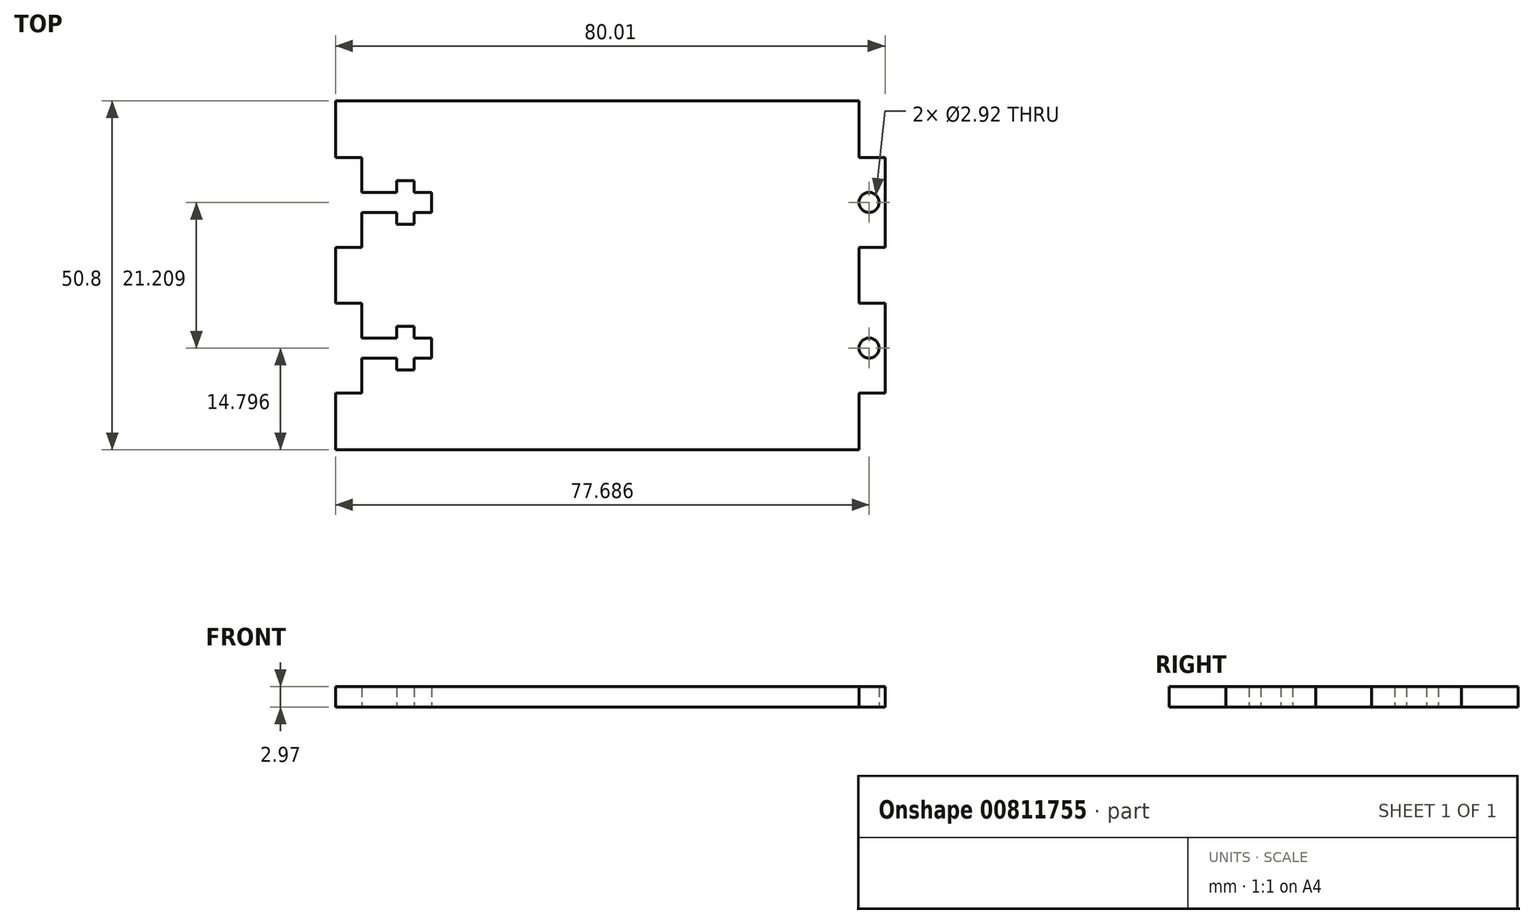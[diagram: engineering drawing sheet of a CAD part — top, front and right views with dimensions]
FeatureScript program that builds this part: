
annotation { "Feature Type Name" : "Feature", "Feature Type Description" : "" }
export const myFeature = defineFeature(function(context is Context, id is Id, definition is map)
    precondition{}
    {
        {
            var Q0;
            Q0=qCreatedBy(makeId("Top.planeOp"),FACE);
            var sketch = newSketch(context, id + "F0", { "sketchPlane" : qUnion([Q0])});
            skLineSegment(sketch, "E0.bottom", {"start": v(0, 0) * mm, "end": v(76.2, 0) * mm});
            skLineSegment(sketch, "E0.top", {"start": v(0, 50.8) * mm, "end": v(76.2, 50.8) * mm});
            skLineSegment(sketch, "E1", {"start": v(0, 8.26) * mm, "end": v(3.81, 8.26) * mm});
            skLineSegment(sketch, "E2", {"start": v(3.81, 8.26) * mm, "end": v(3.81, 13.34) * mm});
            skLineSegment(sketch, "E3", {"start": v(3.81, 13.34) * mm, "end": v(8.9, 13.34) * mm});
            skLineSegment(sketch, "E4", {"start": v(8.9, 13.34) * mm, "end": v(8.9, 11.6) * mm});
            skLineSegment(sketch, "E5", {"start": v(8.9, 11.6) * mm, "end": v(11.43, 11.6) * mm});
            skLineSegment(sketch, "E6", {"start": v(11.43, 11.6) * mm, "end": v(11.43, 13.34) * mm});
            skLineSegment(sketch, "E7", {"start": v(11.43, 13.34) * mm, "end": v(13.97, 13.34) * mm});
            skLineSegment(sketch, "E8", {"start": v(13.97, 13.34) * mm, "end": v(13.97, 16.26) * mm});
            skLineSegment(sketch, "E9", {"start": v(13.97, 16.26) * mm, "end": v(11.43, 16.26) * mm});
            skLineSegment(sketch, "E10", {"start": v(11.43, 16.26) * mm, "end": v(11.43, 17.98) * mm});
            skLineSegment(sketch, "E11", {"start": v(11.43, 17.98) * mm, "end": v(8.9, 17.98) * mm});
            skLineSegment(sketch, "E12", {"start": v(8.9, 17.98) * mm, "end": v(8.9, 16.26) * mm});
            skLineSegment(sketch, "E13", {"start": v(8.9, 16.26) * mm, "end": v(3.81, 16.26) * mm});
            skLineSegment(sketch, "E14", {"start": v(3.81, 16.26) * mm, "end": v(3.81, 21.34) * mm});
            skLineSegment(sketch, "E15", {"start": v(3.81, 21.34) * mm, "end": v(0, 21.34) * mm});
            skLineSegment(sketch, "E16", {"start": v(0, 0) * mm, "end": v(0, 8.26) * mm});
            skLineSegment(sketch, "E17", {"start": v(0, 50.8) * mm, "end": v(0, 42.55) * mm});
            skLineSegment(sketch, "E18", {"start": v(0, 42.55) * mm, "end": v(3.81, 42.55) * mm});
            skLineSegment(sketch, "E19", {"start": v(3.81, 42.54) * mm, "end": v(3.81, 37.46) * mm});
            skLineSegment(sketch, "E20", {"start": v(3.81, 37.46) * mm, "end": v(8.89, 37.46) * mm});
            skLineSegment(sketch, "E21", {"start": v(8.89, 37.46) * mm, "end": v(8.89, 39.2) * mm});
            skLineSegment(sketch, "E22", {"start": v(8.89, 39.2) * mm, "end": v(11.43, 39.2) * mm});
            skLineSegment(sketch, "E23", {"start": v(11.43, 39.2) * mm, "end": v(11.43, 37.46) * mm});
            skLineSegment(sketch, "E24", {"start": v(11.43, 37.46) * mm, "end": v(13.97, 37.46) * mm});
            skLineSegment(sketch, "E25", {"start": v(13.97, 37.46) * mm, "end": v(13.97, 34.54) * mm});
            skLineSegment(sketch, "E26", {"start": v(13.97, 34.54) * mm, "end": v(11.43, 34.54) * mm});
            skLineSegment(sketch, "E27", {"start": v(11.43, 34.54) * mm, "end": v(11.43, 32.82) * mm});
            skLineSegment(sketch, "E28", {"start": v(11.43, 32.82) * mm, "end": v(8.89, 32.82) * mm});
            skLineSegment(sketch, "E29", {"start": v(8.89, 32.82) * mm, "end": v(8.89, 34.54) * mm});
            skLineSegment(sketch, "E30", {"start": v(8.89, 34.54) * mm, "end": v(3.81, 34.54) * mm});
            skLineSegment(sketch, "E31", {"start": v(3.81, 34.54) * mm, "end": v(3.81, 29.46) * mm});
            skLineSegment(sketch, "E32", {"start": v(3.81, 29.46) * mm, "end": v(0, 29.46) * mm});
            skLineSegment(sketch, "E33", {"start": v(0, 29.46) * mm, "end": v(0, 21.34) * mm});
            skLineSegment(sketch, "E34", {"start": v(76.2, 0) * mm, "end": v(76.2, 8.26) * mm});
            skLineSegment(sketch, "E35", {"start": v(76.2, 8.26) * mm, "end": v(80.01, 8.26) * mm});
            skLineSegment(sketch, "E36", {"start": v(80.01, 8.26) * mm, "end": v(80.01, 21.34) * mm});
            skLineSegment(sketch, "E37", {"start": v(80.01, 21.34) * mm, "end": v(76.2, 21.34) * mm});
            skLineSegment(sketch, "E38", {"start": v(76.2, 21.34) * mm, "end": v(76.2, 29.46) * mm});
            skLineSegment(sketch, "E39", {"start": v(76.2, 29.46) * mm, "end": v(80.01, 29.46) * mm});
            skLineSegment(sketch, "E40", {"start": v(80.01, 29.46) * mm, "end": v(80.01, 42.54) * mm});
            skLineSegment(sketch, "E41", {"start": v(80.01, 42.54) * mm, "end": v(76.2, 42.54) * mm});
            skLineSegment(sketch, "E42", {"start": v(76.2, 42.54) * mm, "end": v(76.2, 50.8) * mm});
            skCircle(sketch, "E43", {"center": v(77.69, 14.8) * mm, "radius": 1.46 * mm});
            skCircle(sketch, "E44", {"center": v(77.69, 36) * mm, "radius": 1.46 * mm});
            skSolve(sketch);
        }
        {
            var Q0;
            Q0=makeQuery(id+"F0.imprint","IMPRINT",FACE,{"disambiguationData":[TD([[makeQuery(id+"F0.imprint","IMPRINT",EDGE,{"derivedFrom":sQuery(id+"F0.wireOp",EDGE,"E0.bottom")}),1.0]])]});
            extrude(context, id + "F1", {"entities" : qUnion([Q0]), "depth" : 2.97 * mm, "offsetDistance" : 25.4 * mm});
        }
    });
